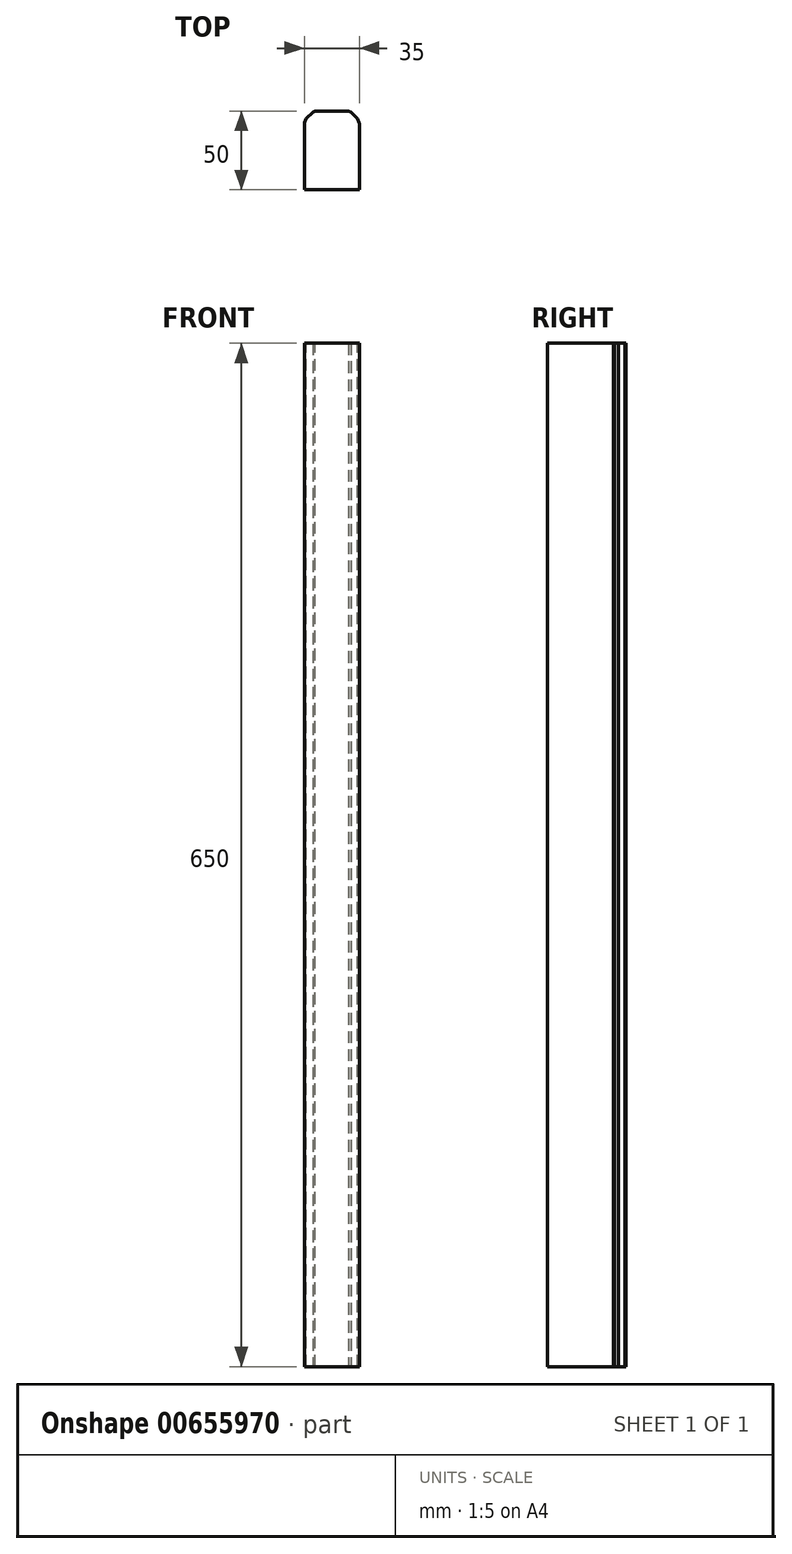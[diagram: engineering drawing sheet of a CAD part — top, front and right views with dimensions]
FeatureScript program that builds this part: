
annotation { "Feature Type Name" : "Feature", "Feature Type Description" : "" }
export const myFeature = defineFeature(function(context is Context, id is Id, definition is map)
    precondition{}
    {
        {
            var Q0;
            Q0=qCreatedBy(makeId("Top.planeOp"),FACE);
            var sketch = newSketch(context, id + "F0", { "sketchPlane" : qUnion([Q0])});
            skLineSegment(sketch, "E0.bottom", {"start": v(17.5, -25) * mm, "end": v(-17.5, -25) * mm});
            skLineSegment(sketch, "E0.top", {"start": v(17.5, 25) * mm, "end": v(-17.5, 25) * mm});
            skLineSegment(sketch, "E0.left", {"start": v(17.5, -25) * mm, "end": v(17.5, 25) * mm});
            skLineSegment(sketch, "E0.right", {"start": v(-17.5, -25) * mm, "end": v(-17.5, 25) * mm});
            skPoint(sketch, "E0.middle", {"position": v(0, 0) * mm});
            skSolve(sketch);
        }
        {
            var Q0;
            Q0=makeQuery(id+"F0.imprint","IMPRINT",FACE,{"disambiguationData":[TD([[makeQuery(id+"F0.imprint","IMPRINT",EDGE,{"derivedFrom":sQuery(id+"F0.wireOp",EDGE,"E0.bottom")}),-1.0]])]});
            extrude(context, id + "F1", {"entities" : qUnion([Q0]), "depth" : 650 * mm, "offsetDistance" : 25 * mm});
        }
        {
            var Q0;
            Q0=makeQuery(id+"F1.opExtrude","SWEPT_EDGE",EDGE,{"disambiguationData":[OSD([sQuery(id+"F0.wireOp",EDGE,"E0.top"),sQuery(id+"F0.wireOp",EDGE,"E0.right")])]});
            var Q1;
            Q1=makeQuery(id+"F1.opExtrude","SWEPT_EDGE",EDGE,{"disambiguationData":[OSD([sQuery(id+"F0.wireOp",EDGE,"E0.top"),sQuery(id+"F0.wireOp",EDGE,"E0.left")])]});
            chamfer(context, id + "F2", {"entities" : qUnion([Q0, Q1]), "width" : 6 * mm, "tangentPropagation" : true});
        }
        {
            var Q0;
            {var subQ0=sQuery(id+"F0.wireOp",EDGE,"E0.right");Q0=makeQuery(id+"F2.opChamfer","BLEND_EDGE",EDGE,{"blendedFrom":[makeQuery(id+"F1.opExtrude","SWEPT_EDGE",EDGE,{"disambiguationData":[OSD([sQuery(id+"F0.wireOp",EDGE,"E0.top"),subQ0])]}),makeQuery(id+"F1.opExtrude","SWEPT_FACE",FACE,{"disambiguationData":[OSD([subQ0])]})],"blendedInto":[makeQuery(id+"F1.opExtrude","SWEPT_FACE",FACE,{"disambiguationData":[OSD([subQ0])]})]});}
            var Q1;
            {var subQ0=sQuery(id+"F0.wireOp",EDGE,"E0.left");Q1=makeQuery(id+"F2.opChamfer","BLEND_EDGE",EDGE,{"blendedFrom":[makeQuery(id+"F1.opExtrude","SWEPT_EDGE",EDGE,{"disambiguationData":[OSD([sQuery(id+"F0.wireOp",EDGE,"E0.top"),subQ0])]}),makeQuery(id+"F1.opExtrude","SWEPT_FACE",FACE,{"disambiguationData":[OSD([subQ0])]})],"blendedInto":[makeQuery(id+"F1.opExtrude","SWEPT_FACE",FACE,{"disambiguationData":[OSD([subQ0])]})]});}
            chamfer(context, id + "F3", {"entities" : qUnion([Q0, Q1]), "width" : 4 * mm, "tangentPropagation" : true});
        }
        {
            var Q0;
            {var subQ0=sQuery(id+"F0.wireOp",EDGE,"E0.top");Q0=makeQuery(id+"F2.opChamfer","BLEND_EDGE",EDGE,{"blendedFrom":[makeQuery(id+"F1.opExtrude","SWEPT_EDGE",EDGE,{"disambiguationData":[OSD([subQ0,sQuery(id+"F0.wireOp",EDGE,"E0.right")])]}),makeQuery(id+"F1.opExtrude","SWEPT_FACE",FACE,{"disambiguationData":[OSD([subQ0])]})],"blendedInto":[makeQuery(id+"F1.opExtrude","SWEPT_FACE",FACE,{"disambiguationData":[OSD([subQ0])]})]});}
            var Q1;
            {var subQ0=sQuery(id+"F0.wireOp",EDGE,"E0.top");Q1=makeQuery(id+"F2.opChamfer","BLEND_EDGE",EDGE,{"blendedFrom":[makeQuery(id+"F1.opExtrude","SWEPT_EDGE",EDGE,{"disambiguationData":[OSD([subQ0,sQuery(id+"F0.wireOp",EDGE,"E0.left")])]}),makeQuery(id+"F1.opExtrude","SWEPT_FACE",FACE,{"disambiguationData":[OSD([subQ0])]})],"blendedInto":[makeQuery(id+"F1.opExtrude","SWEPT_FACE",FACE,{"disambiguationData":[OSD([subQ0])]})]});}
            chamfer(context, id + "F4", {"entities" : qUnion([Q0, Q1]), "width" : 2 * mm, "tangentPropagation" : true});
        }
        {
            var Q0;
            {var subQ0=sQuery(id+"F0.wireOp",EDGE,"E0.right");var subQ1=makeQuery(id+"F1.opExtrude","SWEPT_FACE",FACE,{"disambiguationData":[OSD([subQ0])]});Q0=makeQuery(id+"F3.opChamfer","BLEND_EDGE",EDGE,{"blendedFrom":[makeQuery(id+"F2.opChamfer","BLEND_EDGE",EDGE,{"blendedFrom":[makeQuery(id+"F1.opExtrude","SWEPT_EDGE",EDGE,{"disambiguationData":[OSD([sQuery(id+"F0.wireOp",EDGE,"E0.top"),subQ0])]}),subQ1],"blendedInto":[subQ1]}),subQ1],"blendedInto":[subQ1]});}
            var Q1;
            {var subQ0=sQuery(id+"F0.wireOp",EDGE,"E0.left");var subQ1=makeQuery(id+"F1.opExtrude","SWEPT_FACE",FACE,{"disambiguationData":[OSD([subQ0])]});Q1=makeQuery(id+"F3.opChamfer","BLEND_EDGE",EDGE,{"blendedFrom":[makeQuery(id+"F2.opChamfer","BLEND_EDGE",EDGE,{"blendedFrom":[makeQuery(id+"F1.opExtrude","SWEPT_EDGE",EDGE,{"disambiguationData":[OSD([sQuery(id+"F0.wireOp",EDGE,"E0.top"),subQ0])]}),subQ1],"blendedInto":[subQ1]}),subQ1],"blendedInto":[subQ1]});}
            chamfer(context, id + "F5", {"entities" : qUnion([Q0, Q1]), "width" : 2 * mm, "tangentPropagation" : true});
        }
    });
